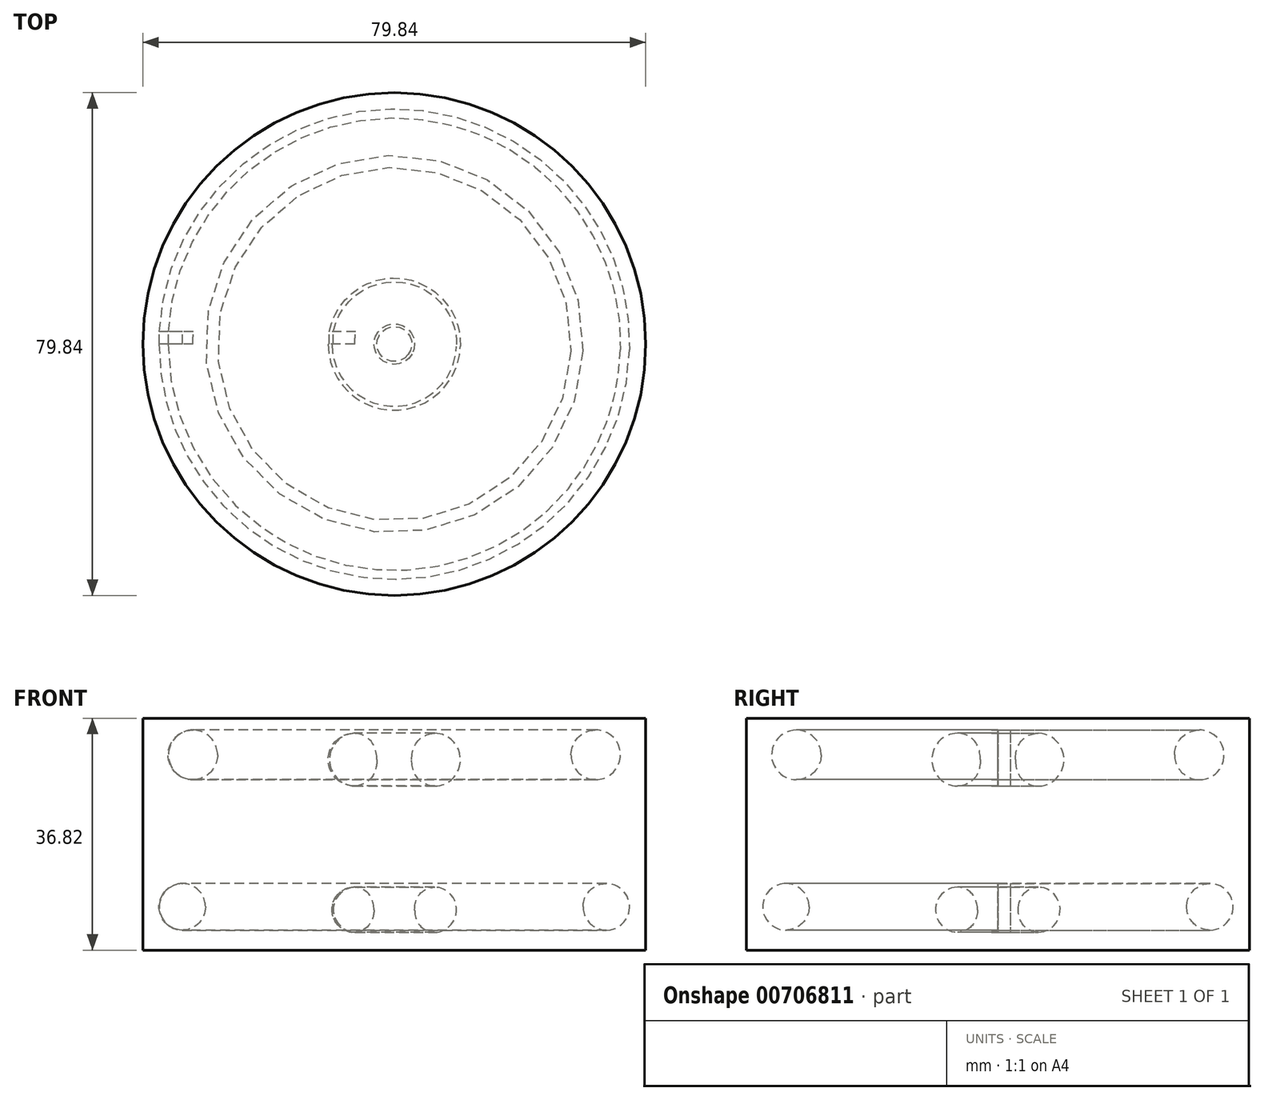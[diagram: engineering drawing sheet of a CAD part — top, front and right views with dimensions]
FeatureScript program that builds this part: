
annotation { "Feature Type Name" : "Feature", "Feature Type Description" : "" }
export const myFeature = defineFeature(function(context is Context, id is Id, definition is map)
    precondition{}
    {
        {
            var Q0;
            Q0=qCreatedBy(makeId("Front.planeOp"),FACE);
            var sketch = newSketch(context, id + "F0", { "sketchPlane" : qUnion([Q0])});
            skLineSegment(sketch, "E0.bottom", {"start": v(0, 0) * mm, "end": v(39.87, 0) * mm});
            skLineSegment(sketch, "E0.top", {"start": v(0, 36.82) * mm, "end": v(39.87, 36.82) * mm});
            skLineSegment(sketch, "E0.left", {"start": v(0, 0) * mm, "end": v(0, 36.82) * mm});
            skLineSegment(sketch, "E0.right", {"start": v(39.87, 0) * mm, "end": v(39.87, 36.82) * mm});
            skCircle(sketch, "E1", {"center": v(7.94, 31.01) * mm, "radius": 3.94 * mm});
            skCircle(sketch, "E2", {"center": v(33.76, 30.25) * mm, "radius": 4.2 * mm});
            skCircle(sketch, "E3", {"center": v(33.76, 6.42) * mm, "radius": 3.58 * mm});
            skCircle(sketch, "E4", {"center": v(6.26, 6.87) * mm, "radius": 3.7 * mm});
            skSolve(sketch);
        }
        {
            var Q0;
            Q0 = qSketchRegion(id + "F0", true);
            extrude(context, id + "F1", {"entities" : qUnion([Q0]), "depth" : 2 * mm, "offsetDistance" : 25 * mm});
        }
        {
            var Q0;
            Q0 = qSketchRegion(id + "F0", true);
            var Q1;
            Q1=makeQuery(id+"F1.opExtrude","SWEPT_FACE",FACE,{"disambiguationData":[OSD([sQuery(id+"F0.wireOp",EDGE,"E0.right")])]});
            var Q2;
            Q2=makeQuery(id+"F1.opExtrude","CAP_EDGE",EDGE,{"disambiguationData":[OSD([sQuery(id+"F0.wireOp",EDGE,"E0.right")])],"isStart":false});
            revolve(context, id + "F2", {"operationType" : NewBodyOperationType.ADD, "surfaceOperationType" : NewSurfaceOperationType.NEW, "entities" : qUnion([Q0, Q1]), "axis" : qUnion([Q2]), "revolveType" : RevolveType.FULL});
        }
    });
